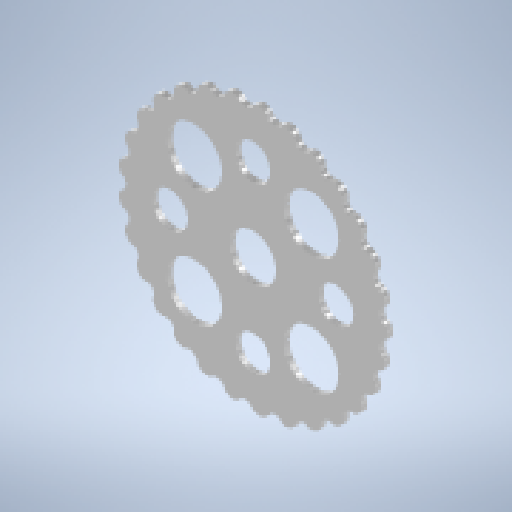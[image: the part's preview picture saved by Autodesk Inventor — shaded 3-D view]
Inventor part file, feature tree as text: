
AUTODESK INVENTOR PART (.ipt)
format: ipt  version: 2024 (Build 280153000, 153)  size: 344,576 bytes
history: native  units: mm
features: sketch x4, extrude x3, other x2, pattern_circular x2, hole x1
ambient origin geometry x8: Origin, YZ Plane, XZ Plane, XY Plane, X Axis, Y Axis, Z Axis, Center Point
bodies: Body1 (feature_tree)
feature tree (12):
  other  "ソリッド1"
  extrude  "押し出し1"  Depth=3600.0mm TaperAngle=0.0deg
  hole  "穴1"  [1 undecoded]
  extrude  "押し出し2"  Depth=19.0mm
  pattern_circular  "円形状パターン1"  [2 undecoded]
  extrude  "押し出し3"  TaperAngle=0.0deg  [1 undecoded]
  pattern_circular  "円形状パターン2"  Count=4 Angle=360.0deg
  sketch  "スケッチ1"
  other  "2D 計算式曲線1"
  sketch  "スケッチ2"
  sketch  "スケッチ3"
  sketch  "スケッチ4"
note: 4 required parameter values undecoded (feature->parameter linkage not recoverable at this tier; creation-order binding heuristic only, values carry confidence <= 0.55)
